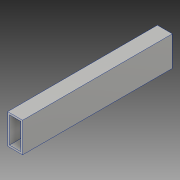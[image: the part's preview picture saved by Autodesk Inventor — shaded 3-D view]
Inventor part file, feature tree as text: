
AUTODESK INVENTOR PART (.ipt)
format: ipt  version: 2019 (Build 230136000, 136)  size: 91,136 bytes
history: native  units: in
note: dims shown in document units (in); Inventor stores cm internally (conversion verified against a paired STEP export)
features: extrude x1, sketch x1
ambient origin geometry x8: Origin, YZ Plane, XZ Plane, XY Plane, X Axis, Y Axis, Z Axis, Center Point
bodies: Solid1 (feature_tree)
feature tree (2):
  extrude  "Extrusion1"  [1 undecoded]
  sketch  "Sketch1"  dims[d4=0.0in]
note: 1 required parameter value undecoded (feature->parameter linkage not recoverable at this tier; creation-order binding heuristic only, values carry confidence <= 0.55)
